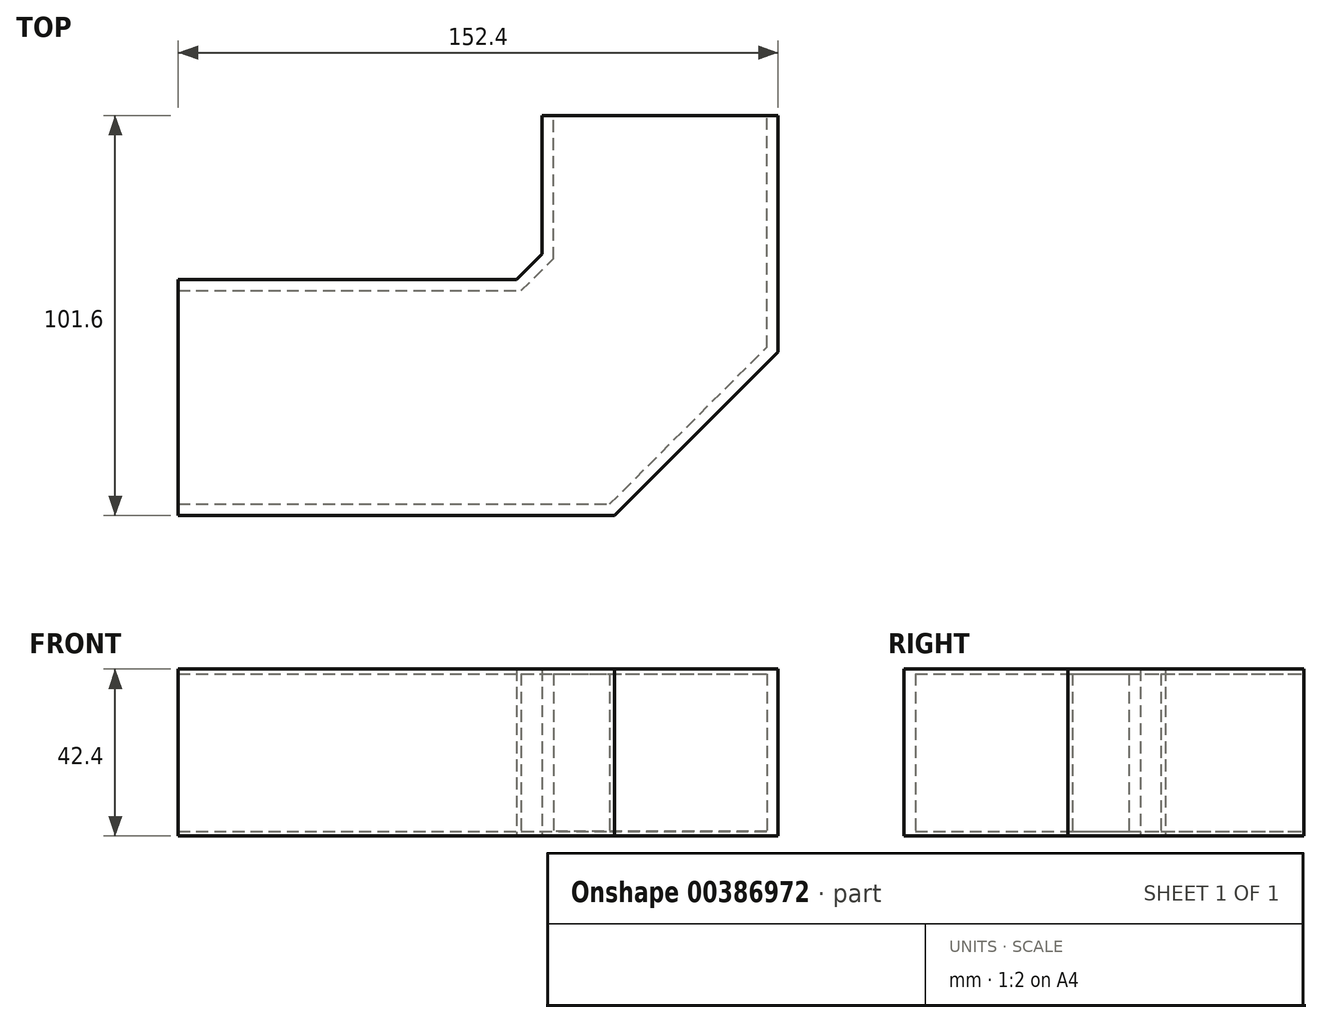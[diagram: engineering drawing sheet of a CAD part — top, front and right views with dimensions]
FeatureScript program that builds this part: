
annotation { "Feature Type Name" : "Feature", "Feature Type Description" : "" }
export const myFeature = defineFeature(function(context is Context, id is Id, definition is map)
    precondition{}
    {
        {
            var Q0;
            Q0=qCreatedBy(makeId("Top.planeOp"),FACE);
            var sketch = newSketch(context, id + "F0", { "sketchPlane" : qUnion([Q0])});
            skLineSegment(sketch, "E0.bottom", {"start": v(0, 0) * mm, "end": v(110.8, 0) * mm});
            skLineSegment(sketch, "E0.top", {"start": v(0, 60) * mm, "end": v(85.95, 60) * mm});
            skLineSegment(sketch, "E0.left", {"start": v(0, 0) * mm, "end": v(0, 60) * mm});
            skLineSegment(sketch, "E1.top", {"start": v(152.4, 101.6) * mm, "end": v(92.4, 101.6) * mm});
            skLineSegment(sketch, "E1.right", {"start": v(92.4, 66.45) * mm, "end": v(92.4, 101.6) * mm});
            skLineSegment(sketch, "E2", {"start": v(110.8, 0) * mm, "end": v(152.4, 41.6) * mm});
            skLineSegment(sketch, "E3", {"start": v(152.4, 41.6) * mm, "end": v(152.4, 101.6) * mm});
            skLineSegment(sketch, "E4", {"start": v(85.95, 60) * mm, "end": v(92.4, 66.45) * mm});
            skSolve(sketch);
        }
        {
            var Q0;
            Q0=makeQuery(id+"F0.imprint","IMPRINT",FACE,{"disambiguationData":[TD([[makeQuery(id+"F0.imprint","IMPRINT",EDGE,{"derivedFrom":sQuery(id+"F0.wireOp",EDGE,"E0.bottom")}),1.0]])]});
            extrude(context, id + "F1", {"entities" : qUnion([Q0]), "depth" : 1.2 * mm});
        }
        {
            var Q0;
            Q0=makeQuery(id+"F1.opExtrude","CAP_FACE",FACE,{"disambiguationData":[OSD([sQuery(id+"F0.wireOp",EDGE,"E0.bottom"),sQuery(id+"F0.wireOp",EDGE,"E0.top"),sQuery(id+"F0.wireOp",EDGE,"E0.left"),sQuery(id+"F0.wireOp",EDGE,"E1.top"),sQuery(id+"F0.wireOp",EDGE,"E1.right"),sQuery(id+"F0.wireOp",EDGE,"E2"),sQuery(id+"F0.wireOp",EDGE,"E3"),sQuery(id+"F0.wireOp",EDGE,"E4")])],"isStart":false});
            var sketch = newSketch(context, id + "F2", { "sketchPlane" : qUnion([Q0])});
            skLineSegment(sketch, "E5.0.2", {"start": v(0, 2.88) * mm, "end": v(0, 0) * mm});
            skLineSegment(sketch, "E5.0.3", {"start": v(0, 0) * mm, "end": v(110.8, 0) * mm});
            skLineSegment(sketch, "E5.0.4", {"start": v(110.8, 0) * mm, "end": v(152.4, 41.6) * mm});
            skLineSegment(sketch, "E5.0.5", {"start": v(152.4, 41.6) * mm, "end": v(152.4, 101.6) * mm});
            skLineSegment(sketch, "E5.0.6", {"start": v(152.4, 101.6) * mm, "end": v(149.52, 101.6) * mm});
            skLineSegment(sketch, "E6.0", {"start": v(149.52, 42.8) * mm, "end": v(149.52, 101.6) * mm});
            skLineSegment(sketch, "E6.1", {"start": v(109.6, 2.88) * mm, "end": v(149.52, 42.8) * mm});
            skLineSegment(sketch, "E6.2", {"start": v(0, 2.88) * mm, "end": v(109.6, 2.88) * mm});
            skPoint(sketch, "E5.0.1.end.orphan", {"position": v(0, 60) * mm});
            skPoint(sketch, "E5.0.0.end.orphan", {"position": v(85.95, 60) * mm});
            skPoint(sketch, "E5.0.7.end.orphan", {"position": v(92.4, 66.45) * mm});
            skPoint(sketch, "E7.orphan", {"position": v(92.4, 101.6) * mm});
            skSolve(sketch);
        }
        {
            var Q0;
            {var subQ2=sQuery(id+"F2.wireOp",EDGE,"E6.0");Q0=makeQuery(id+"F2.imprint","IMPRINT",FACE,{"disambiguationData":[TD([[makeQuery(id+"F2.imprint","IMPRINT",EDGE,{"derivedFrom":subQ2}),1.0]])]});}
            var sketch = newSketch(context, id + "F3", { "sketchPlane" : qUnion([Q0])});
            skLineSegment(sketch, "E8.0", {"start": v(0, 60) * mm, "end": v(85.95, 60) * mm});
            skLineSegment(sketch, "E9.0", {"start": v(85.95, 60) * mm, "end": v(92.4, 66.45) * mm});
            skLineSegment(sketch, "E10.0", {"start": v(92.4, 66.45) * mm, "end": v(92.4, 101.6) * mm});
            skLineSegment(sketch, "E11.0", {"start": v(95.28, 65.26) * mm, "end": v(95.28, 101.6) * mm});
            skLineSegment(sketch, "E11.1", {"start": v(87.14, 57.12) * mm, "end": v(95.28, 65.26) * mm});
            skLineSegment(sketch, "E11.2", {"start": v(0, 57.12) * mm, "end": v(87.14, 57.12) * mm});
            skLineSegment(sketch, "E12", {"start": v(0, 57.12) * mm, "end": v(0, 60) * mm});
            skLineSegment(sketch, "E13", {"start": v(95.28, 101.6) * mm, "end": v(92.4, 101.6) * mm});
            skSolve(sketch);
        }
        {
            var Q0;
            Q0 = qSketchRegion(id + "F2", true);
            var Q1;
            Q1=makeQuery(id+"F3.imprint","IMPRINT",FACE,{"disambiguationData":[TD([[makeQuery(id+"F3.imprint","IMPRINT",EDGE,{"derivedFrom":sQuery(id+"F3.wireOp",EDGE,"E8.0")}),-1.0]])]});
            extrude(context, id + "F4", {"entities" : qUnion([Q0, Q1]), "operationType" : NewBodyOperationType.ADD, "depth" : 40 * mm});
        }
        {
            var Q0;
            Q0=makeQuery(id+"F4.opExtrude","CAP_FACE",FACE,{"disambiguationData":[OSD([sQuery(id+"F2.wireOp",EDGE,"E5.0.3"),sQuery(id+"F2.wireOp",EDGE,"E5.0.4"),sQuery(id+"F2.wireOp",EDGE,"E5.0.5"),sQuery(id+"F2.wireOp",EDGE,"E6.0"),sQuery(id+"F2.wireOp",EDGE,"E6.1"),sQuery(id+"F2.wireOp",EDGE,"E6.2"),sQuery(id+"F2.wireOp",EDGE,"E5.0.2"),sQuery(id+"F2.wireOp",EDGE,"E5.0.6")])],"isStart":false});
            var sketch = newSketch(context, id + "F5", { "sketchPlane" : qUnion([Q0])});
            skLineSegment(sketch, "E14.0.0", {"start": v(85.95, 60) * mm, "end": v(92.4, 66.45) * mm});
            skLineSegment(sketch, "E14.0.1", {"start": v(92.4, 66.45) * mm, "end": v(92.4, 101.6) * mm});
            skLineSegment(sketch, "E14.0.2", {"start": v(92.4, 101.6) * mm, "end": v(152.4, 101.6) * mm});
            skLineSegment(sketch, "E14.0.3", {"start": v(152.4, 101.6) * mm, "end": v(152.4, 41.6) * mm});
            skLineSegment(sketch, "E14.0.4", {"start": v(152.4, 41.6) * mm, "end": v(110.8, 0) * mm});
            skLineSegment(sketch, "E14.0.5", {"start": v(110.8, 0) * mm, "end": v(0, 0) * mm});
            skLineSegment(sketch, "E14.0.6", {"start": v(0, 0) * mm, "end": v(0, 60) * mm});
            skLineSegment(sketch, "E14.0.7", {"start": v(0, 60) * mm, "end": v(85.95, 60) * mm});
            skSolve(sketch);
        }
        {
            var Q0;
            Q0 = qSketchRegion(id + "F5", true);
            extrude(context, id + "F6", {"entities" : qUnion([Q0]), "operationType" : NewBodyOperationType.ADD, "depth" : 1.2 * mm});
        }
    });
